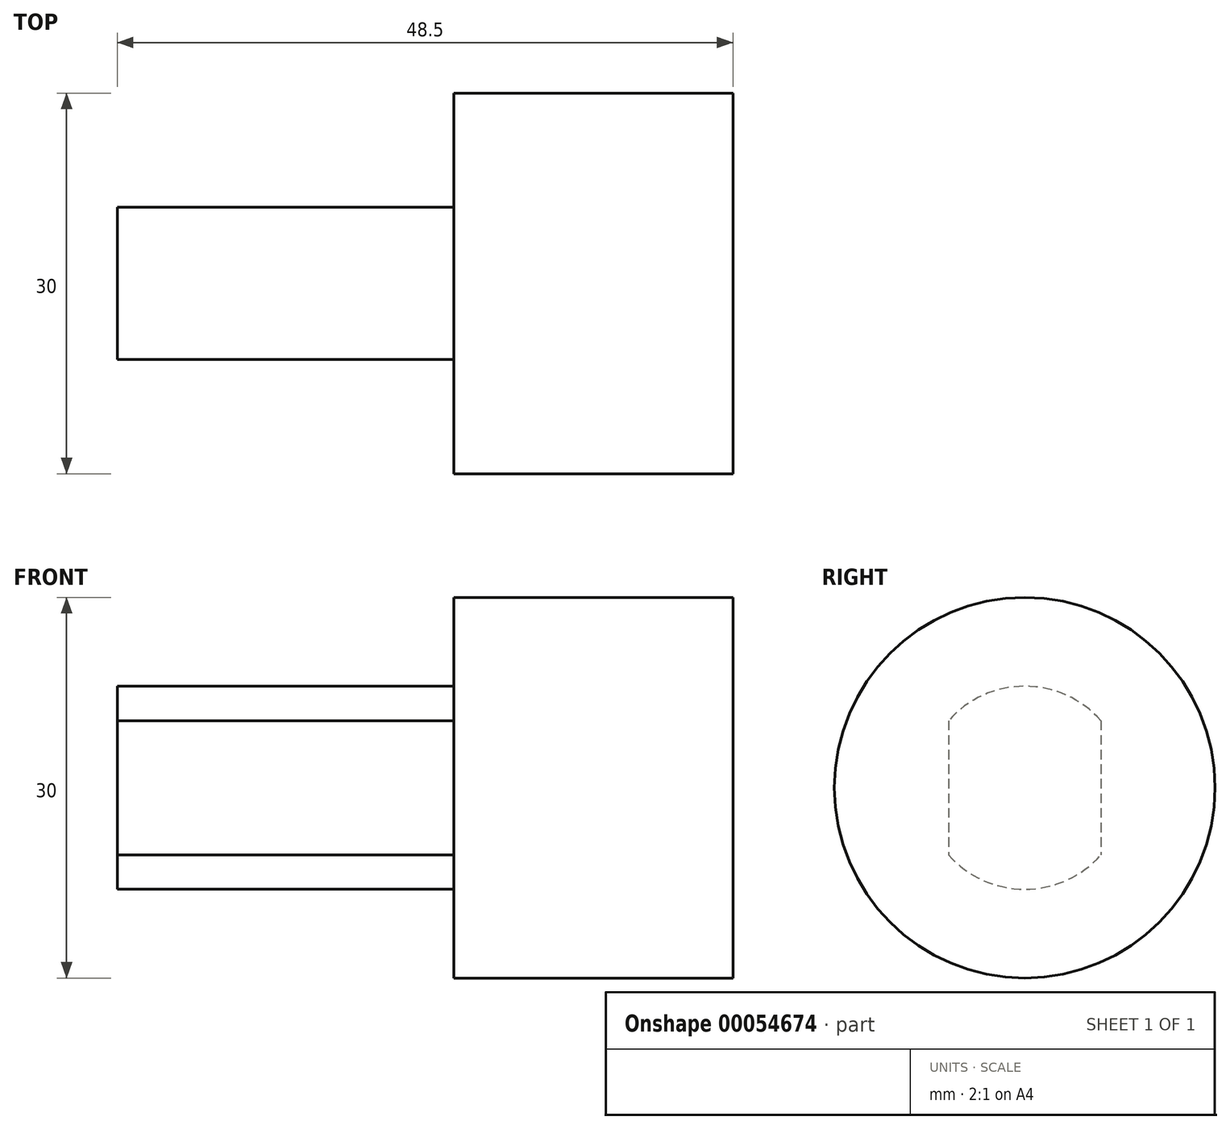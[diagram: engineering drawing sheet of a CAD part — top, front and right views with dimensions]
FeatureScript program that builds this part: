
annotation { "Feature Type Name" : "Feature", "Feature Type Description" : "" }
export const myFeature = defineFeature(function(context is Context, id is Id, definition is map)
    precondition{}
    {
        {
            var Q0;
            Q0=qCreatedBy(makeId("Right.planeOp"),FACE);
            var sketch = newSketch(context, id + "F0", { "sketchPlane" : qUnion([Q0])});
            skPoint(sketch, "E0", {"position": v(0, 0) * mm});
            skCircle(sketch, "E1", {"center": v(0, 0) * mm, "radius": 15 * mm});
            skArc(sketch, "E2", {"start": v(-6, -5.3) * mm, "mid": v(0, -8) * mm, "end": v(6, -5.3) * mm});
            skLineSegment(sketch, "E3", {"start": v(6, 5.3) * mm, "end": v(6, -5.3) * mm});
            skLineSegment(sketch, "E4", {"start": v(-6, 5.3) * mm, "end": v(-6, -5.3) * mm});
            skArc(sketch, "E5.trimOffspring", {"start": v(6, 5.3) * mm, "mid": v(0, 8) * mm, "end": v(-6, 5.3) * mm});
            skSolve(sketch);
        }
        {
            var Q0;
            Q0=makeQuery(id+"F0.imprint","IMPRINT",FACE,{"disambiguationData":[TD([[makeQuery(id+"F0.imprint","IMPRINT",EDGE,{"derivedFrom":sQuery(id+"F0.wireOp",EDGE,"E2")}),1.0]])]});
            var Q1;
            Q1=makeQuery(id+"F0.imprint","IMPRINT",FACE,{"disambiguationData":[TD([[makeQuery(id+"F0.imprint","IMPRINT",EDGE,{"derivedFrom":sQuery(id+"F0.wireOp",EDGE,"E1")}),1.0]])]});
            extrude(context, id + "F1", {"entities" : qUnion([Q0, Q1]), "depth" : 22 * mm});
        }
        {
            var Q0;
            Q0=makeQuery(id+"F0.imprint","IMPRINT",FACE,{"disambiguationData":[TD([[makeQuery(id+"F0.imprint","IMPRINT",EDGE,{"derivedFrom":sQuery(id+"F0.wireOp",EDGE,"E2")}),1.0]])]});
            extrude(context, id + "F2", {"entities" : qUnion([Q0]), "operationType" : NewBodyOperationType.ADD, "oppositeDirection" : true, "depth" : 26.5 * mm});
        }
    });
